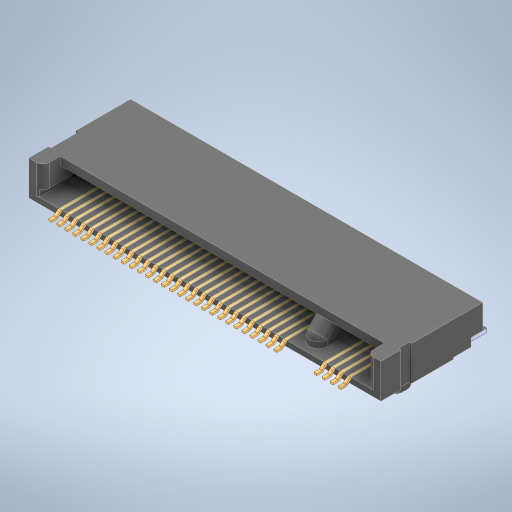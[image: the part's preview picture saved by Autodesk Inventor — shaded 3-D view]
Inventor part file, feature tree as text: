
AUTODESK INVENTOR PART (.ipt)
format: ipt  version: 2024 (Build 280153000, 153)  size: 1,395,712 bytes
history: native  units: in
note: dims shown in document units (in); Inventor stores cm internally (conversion verified against a paired STEP export)
features: other x71, sketch x32, mirror x1
ambient origin geometry x8: Origin, YZ Plane, XZ Plane, XY Plane, X Axis, Y Axis, Z Axis, Center Point
bodies: Solid1 (feature_tree), Solid2 (feature_tree), Solid3 (feature_tree), Solid4 (feature_tree), Solid5 (feature_tree), Solid6 (feature_tree), Solid7 (feature_tree), Solid8 (feature_tree), Solid9 (feature_tree), Solid10 (feature_tree), Solid11 (feature_tree), Solid12 (feature_tree), Solid13 (feature_tree), Solid14 (feature_tree), Solid15 (feature_tree), Solid16 (feature_tree), Solid17 (feature_tree), Solid18 (feature_tree), Solid19 (feature_tree), Solid20 (feature_tree), Solid21 (feature_tree), Solid22 (feature_tree), Solid23 (feature_tree), Solid24 (feature_tree), Solid25 (feature_tree), Solid26 (feature_tree), Solid27 (feature_tree), Solid28 (feature_tree), Solid29 (feature_tree), Solid30 (feature_tree), Solid31 (feature_tree), Solid32 (feature_tree), Solid33 (feature_tree), Solid34 (feature_tree), Solid35 (feature_tree), Solid36 (feature_tree), Solid37 (feature_tree), Solid38 (feature_tree), Solid39 (feature_tree), Solid40 (feature_tree), Solid41 (feature_tree), Solid42 (feature_tree), Solid43 (feature_tree), Solid44 (feature_tree), Solid45 (feature_tree), Solid46 (feature_tree), Solid47 (feature_tree), Solid48 (feature_tree), Solid49 (feature_tree), Solid50 (feature_tree), Solid51 (feature_tree), Solid52 (feature_tree), Solid53 (feature_tree), Solid54 (feature_tree), Solid55 (feature_tree), Solid56 (feature_tree), Solid57 (feature_tree), Solid58 (feature_tree), Solid59 (feature_tree), Solid60 (feature_tree), Solid61 (feature_tree), Solid62 (feature_tree), Solid63 (feature_tree), Solid64 (feature_tree), Solid65 (feature_tree), Solid66 (feature_tree), Solid67 (feature_tree), Solid68 (feature_tree), Solid69 (feature_tree), Solid70 (feature_tree), Solid71 (feature_tree), Solid72 (feature_tree), Solid73 (feature_tree), Solid74 (feature_tree), Solid75 (feature_tree), Solid76 (feature_tree), Solid77 (feature_tree), Solid78 (feature_tree), Solid79 (feature_tree), Solid80 (feature_tree), Solid81 (feature_tree), Solid82 (feature_tree), Solid83 (feature_tree), Solid84 (feature_tree), Solid85 (feature_tree), Solid86 (feature_tree), Solid87 (feature_tree), Solid88 (feature_tree), Solid89 (feature_tree), Solid90 (feature_tree), Solid91 (feature_tree), Solid92 (feature_tree), Solid93 (feature_tree), Solid94 (feature_tree), Solid95 (feature_tree), Solid96 (feature_tree), Solid97 (feature_tree), Solid98 (feature_tree), Solid99 (feature_tree), Solid100 (feature_tree), Solid101 (feature_tree), Solid102 (feature_tree), Solid103 (feature_tree), Solid104 (feature_tree)
feature tree (104):
  other  "Housing"
  other  "Pin 2"
  sketch  "Sketch-Pattern1[1]"
  sketch  "Sketch-Pattern1[2]"
  sketch  "Sketch-Pattern1[3]"
  sketch  "Sketch-Pattern1[4]"
  sketch  "Sketch-Pattern1[5]"
  sketch  "Sketch-Pattern1[6]"
  sketch  "Sketch-Pattern1[7]"
  sketch  "Sketch-Pattern1[8]"
  sketch  "Sketch-Pattern1[9]"
  sketch  "Sketch-Pattern1[10]"
  sketch  "Sketch-Pattern1[11]"
  sketch  "Sketch-Pattern1[12]"
  sketch  "Sketch-Pattern1[13]"
  sketch  "Sketch-Pattern1[14]"
  sketch  "Sketch-Pattern1[15]"
  sketch  "Sketch-Pattern1[16]"
  sketch  "Sketch-Pattern1[17]"
  sketch  "Sketch-Pattern1[18]"
  sketch  "Sketch-Pattern1[19]"
  sketch  "Sketch-Pattern1[20]"
  sketch  "Sketch-Pattern1[21]"
  sketch  "Sketch-Pattern1[22]"
  sketch  "Sketch-Pattern1[23]"
  sketch  "Sketch-Pattern1[24]"
  sketch  "Sketch-Pattern1[25]"
  sketch  "Sketch-Pattern1[26]"
  sketch  "Sketch-Pattern1[27]"
  sketch  "Sketch-Pattern1[28]"
  sketch  "Sketch-Pattern1[29]"
  sketch  "Sketch-Pattern1[30]"
  sketch  "Sketch-Pattern1[31]"
  sketch  "Sketch-Pattern1[32]"
  other  "Pin 1"
  other  "LPattern3[1]"
  other  "LPattern3[2]"
  other  "LPattern3[3]"
  other  "LPattern3[4]"
  other  "LPattern3[5]"
  other  "LPattern3[6]"
  other  "LPattern3[7]"
  other  "LPattern3[8]"
  other  "LPattern3[9]"
  other  "LPattern3[10]"
  other  "LPattern3[11]"
  other  "LPattern3[12]"
  other  "LPattern3[13]"
  other  "LPattern3[14]"
  other  "LPattern3[15]"
  other  "LPattern3[16]"
  other  "LPattern3[17]"
  other  "LPattern3[18]"
  other  "LPattern3[19]"
  other  "LPattern3[20]"
  other  "LPattern3[21]"
  other  "LPattern3[22]"
  other  "LPattern3[23]"
  other  "LPattern3[24]"
  other  "LPattern3[25]"
  other  "LPattern3[26]"
  other  "LPattern3[27]"
  other  "LPattern3[28]"
  other  "Boss-Extrude8[1]"
  other  "LPattern4[1]"
  other  "LPattern4[2]"
  other  "LPattern4[3]"
  other  "LPattern4[4]"
  other  "Boss-Extrude8[2]"
  other  "LPattern4[5]"
  other  "LPattern4[6]"
  other  "LPattern4[7]"
  other  "LPattern4[8]"
  other  "Contact 1"
  other  "LPattern3[29]"
  other  "LPattern3[30]"
  other  "LPattern3[31]"
  other  "LPattern3[32]"
  other  "LPattern3[33]"
  other  "LPattern3[34]"
  other  "LPattern3[35]"
  other  "LPattern3[36]"
  other  "LPattern3[37]"
  other  "LPattern3[38]"
  other  "LPattern3[39]"
  other  "LPattern3[40]"
  other  "LPattern3[41]"
  other  "LPattern3[42]"
  other  "LPattern3[43]"
  other  "LPattern3[44]"
  other  "LPattern3[45]"
  other  "LPattern3[46]"
  other  "LPattern3[47]"
  other  "LPattern3[48]"
  other  "LPattern3[49]"
  other  "LPattern3[50]"
  other  "LPattern3[51]"
  other  "LPattern3[52]"
  other  "LPattern3[53]"
  other  "LPattern3[54]"
  other  "LPattern3[55]"
  other  "LPattern3[56]"
  other  "Boss-Extrude9"
  mirror  "Mirror1"
